# Revit family: QF_Fisher_75395_Reel_SS_EXP_50_SV
name_source: partatom
category: Specialty Equipment
revit_build: Autodesk Revit 2018 (Build: 20170223_1515(x64)
units: mm (PartAtom-declared; Revit-internal decimal feet)

## family parameters
Always vertical = Yes
Cut with Voids When Loaded = No
Part Type = Normal
Room Calculation Point = No
Round Connector Dimension = Use Diameter
Shared = No
Work Plane-Based = No

## types (1)
- QF_Fisher_75395_Reel_SS_EXP_50_SV
    Cold Water Connection Height = 0"
    Cold Water Flow = 3 GPM
    Cold Water Maximum Pressure = 200.00 psi
    Cold Water Minimum Pressure = 80.00 psi
    Cold Water RI Height = 0"
    Cold Water Size = 1"
    Cold Water Temperature Recommended = 40 °F
    Depth = 20 1/8"
    Description = Reel EXP 50 SV With Pro Spray Valve
    Fixture Finish = QF_Metal_Stainless_Polished
    Foodservice Equipment Identifier = Yes
    Height = 20 1/4"
    Identify Quantity as Lot = Yes
    Length = 6 3/4"
    Manufacturer = FISHER
    Model = 75395
    Weight in Pounds = 52

## geometry (parser evidence)
native form markers: Sweep x2
no freeform markers — native parametric forms only
